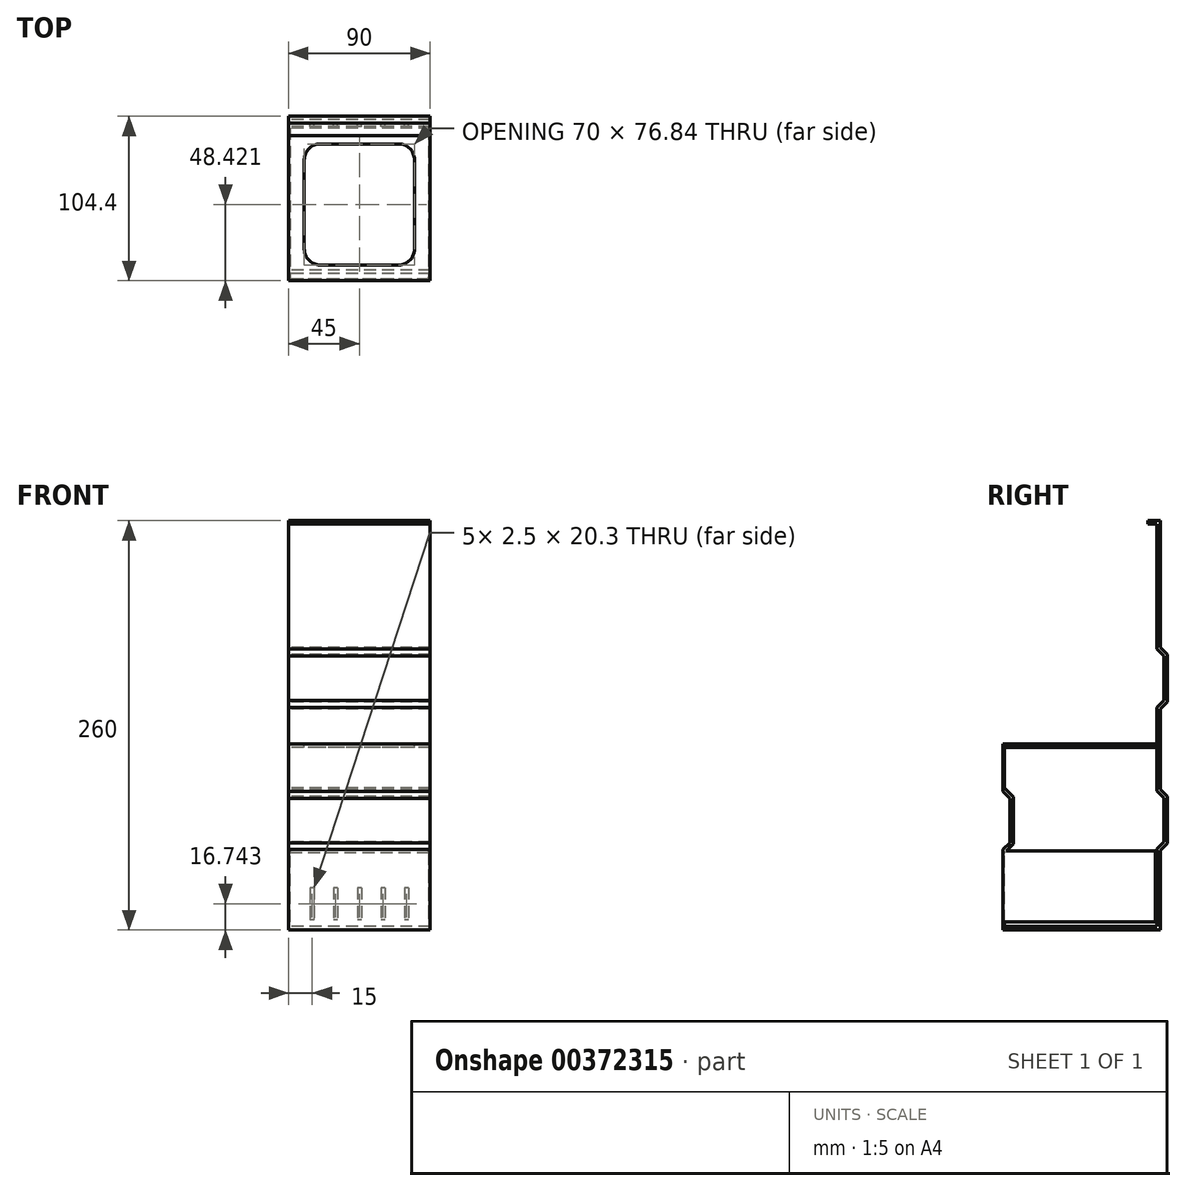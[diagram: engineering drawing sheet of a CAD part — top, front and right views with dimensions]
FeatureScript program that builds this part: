
annotation { "Feature Type Name" : "Feature", "Feature Type Description" : "" }
export const myFeature = defineFeature(function(context is Context, id is Id, definition is map)
    precondition{}
    {
        {
            var Q0;
            Q0=qCreatedBy(makeId("Right.planeOp"),FACE);
            var sketch = newSketch(context, id + "F0", { "sketchPlane" : qUnion([Q0])});
            skLineSegment(sketch, "E0.0", {"start": v(-66.12, 74.6) * mm, "end": v(-66.12, 46.42) * mm});
            skLineSegment(sketch, "E0.1", {"start": v(-63.92, 75.5) * mm, "end": v(-63.92, 45.5) * mm});
            skLineSegment(sketch, "E0.5", {"start": v(-70.52, 132.02) * mm, "end": v(-70.52, 79) * mm});
            skLineSegment(sketch, "E0.7", {"start": v(-68.32, 240.5) * mm, "end": v(-68.32, 169.9) * mm});
            skLineSegment(sketch, "E0.8", {"start": v(-66.12, 164.6) * mm, "end": v(-66.12, 136.42) * mm});
            skLineSegment(sketch, "E0.9", {"start": v(-63.92, 165.5) * mm, "end": v(-63.92, 135.5) * mm});
            skLineSegment(sketch, "E1.4", {"start": v(-68.32, 131.1) * mm, "end": v(-68.32, 79.9) * mm});
            skLineSegment(sketch, "E1.9", {"start": v(-70.52, 238.3) * mm, "end": v(-70.52, 169) * mm});
            skLineSegment(sketch, "E2.0", {"start": v(-63.92, 75.5) * mm, "end": v(-68.32, 79.9) * mm});
            skLineSegment(sketch, "E3.0", {"start": v(-66.12, 74.6) * mm, "end": v(-70.52, 79) * mm});
            skLineSegment(sketch, "E4.0", {"start": v(-68.32, 41.1) * mm, "end": v(-63.92, 45.5) * mm});
            skLineSegment(sketch, "E5.0", {"start": v(-66.12, 136.42) * mm, "end": v(-70.52, 132.02) * mm});
            skLineSegment(sketch, "E6.0", {"start": v(-63.92, 135.5) * mm, "end": v(-68.32, 131.1) * mm});
            skLineSegment(sketch, "E7.0", {"start": v(-68.32, 169.9) * mm, "end": v(-63.92, 165.5) * mm});
            skLineSegment(sketch, "E8.0", {"start": v(-70.52, 169) * mm, "end": v(-66.12, 164.6) * mm});
            skLineSegment(sketch, "E9", {"start": v(-66.12, 46.42) * mm, "end": v(-70.52, 42.02) * mm});
            skLineSegment(sketch, "E10.left", {"start": v(-168.32, -9.5) * mm, "end": v(-168.32, 41.61) * mm});
            skLineSegment(sketch, "E10.right", {"start": v(-167.32, -9.5) * mm, "end": v(-167.32, 42.61) * mm});
            skLineSegment(sketch, "E11.4", {"start": v(-161.72, 75.1) * mm, "end": v(-161.72, 45.1) * mm});
            skLineSegment(sketch, "E11.6", {"start": v(-163.92, 74.2) * mm, "end": v(-163.92, 46.01) * mm});
            skLineSegment(sketch, "E12.0", {"start": v(-166.12, 40.7) * mm, "end": v(-161.72, 45.1) * mm});
            skLineSegment(sketch, "E13.0", {"start": v(-168.32, 41.61) * mm, "end": v(-163.92, 46.01) * mm});
            skLineSegment(sketch, "E14.0", {"start": v(-163.92, 74.2) * mm, "end": v(-168.32, 78.6) * mm});
            skLineSegment(sketch, "E15.0", {"start": v(-161.72, 75.1) * mm, "end": v(-166.12, 79.5) * mm});
            skLineSegment(sketch, "E16", {"start": v(-166.12, 79.5) * mm, "end": v(-168.32, 81.7) * mm});
            skLineSegment(sketch, "E17", {"start": v(-166.12, 40.7) * mm, "end": v(-168.32, 38.48) * mm});
            skLineSegment(sketch, "E18.trimOffspring", {"start": v(-167.32, 77.6) * mm, "end": v(-167.32, 108.73) * mm});
            skLineSegment(sketch, "E19.trimOffspring", {"start": v(-168.32, 78.6) * mm, "end": v(-168.32, 108.73) * mm});
            skLineSegment(sketch, "E20", {"start": v(-68.32, 41.1) * mm, "end": v(-68.32, -9.5) * mm});
            skLineSegment(sketch, "E21.bottom", {"start": v(-68.32, -9.5) * mm, "end": v(-168.32, -9.5) * mm});
            skLineSegment(sketch, "E21.top", {"start": v(-68.32, -7.3) * mm, "end": v(-168.32, -7.3) * mm});
            skLineSegment(sketch, "E21.left", {"start": v(-68.32, -9.5) * mm, "end": v(-68.32, -7.3) * mm});
            skLineSegment(sketch, "E21.right", {"start": v(-168.32, -9.5) * mm, "end": v(-168.32, -7.3) * mm});
            skLineSegment(sketch, "E22", {"start": v(-70.52, 42.02) * mm, "end": v(-70.52, -9.5) * mm});
            skLineSegment(sketch, "E23", {"start": v(-168.32, 108.73) * mm, "end": v(-71.48, 108.73) * mm});
            skLineSegment(sketch, "E24", {"start": v(-168.32, 106.53) * mm, "end": v(-71.48, 106.53) * mm});
            skLineSegment(sketch, "E25", {"start": v(-71.48, 106.53) * mm, "end": v(-71.48, 108.73) * mm});
            skLineSegment(sketch, "E26", {"start": v(-50.44, 240.5) * mm, "end": v(-50.44, 250.5) * mm, "construction": true});
            skLineSegment(sketch, "E27", {"start": v(-50.44, 250.5) * mm, "end": v(-80.83, 250.5) * mm, "construction": true});
            skLineSegment(sketch, "E28", {"start": v(-68.32, 250.5) * mm, "end": v(-68.32, 240.5) * mm});
            skLineSegment(sketch, "E29", {"start": v(-70.52, 250.5) * mm, "end": v(-70.52, 238.3) * mm});
            skLineSegment(sketch, "E30.bottom", {"start": v(-76.32, 250.5) * mm, "end": v(-76.32, 250.5) * mm});
            skLineSegment(sketch, "E30.top", {"start": v(-76.32, 248.3) * mm, "end": v(-76.32, 248.3) * mm});
            skLineSegment(sketch, "E30.left", {"start": v(-76.32, 250.5) * mm, "end": v(-76.32, 248.3) * mm, "construction": true});
            skLineSegment(sketch, "E30.right", {"start": v(-76.32, 250.5) * mm, "end": v(-76.32, 248.3) * mm, "construction": true});
            skLineSegment(sketch, "E31.bottom", {"start": v(-76.32, 248.3) * mm, "end": v(-68.32, 248.3) * mm});
            skLineSegment(sketch, "E31.top", {"start": v(-76.32, 250.5) * mm, "end": v(-68.32, 250.5) * mm});
            skLineSegment(sketch, "E31.left", {"start": v(-76.32, 248.3) * mm, "end": v(-76.32, 250.5) * mm});
            skLineSegment(sketch, "E31.right", {"start": v(-68.32, 248.3) * mm, "end": v(-68.32, 250.5) * mm});
            skSolve(sketch);
        }
        {
            var Q0;
            Q0 = qSketchRegion(id + "F0", true);
            extrude(context, id + "F1", {"entities" : qUnion([Q0]), "depth" : 90 * mm, "offsetDistance" : 25 * mm});
        }
        {
            var Q0;
            Q0=makeQuery(id+"F1.opExtrude","SWEPT_FACE",FACE,{"disambiguationData":[OSD([sQuery(id+"F0.wireOp",EDGE,"E10.right")])]});
            var sketch = newSketch(context, id + "F2", { "sketchPlane" : qUnion([Q0])});
            skLineSegment(sketch, "E32.bottom", {"start": v(-90, 40.7) * mm, "end": v(-89, 40.7) * mm});
            skLineSegment(sketch, "E32.top", {"start": v(-90, -4.3) * mm, "end": v(-89, -4.3) * mm});
            skLineSegment(sketch, "E32.left", {"start": v(-90, 40.7) * mm, "end": v(-90, -4.3) * mm});
            skLineSegment(sketch, "E32.right", {"start": v(-89, 40.7) * mm, "end": v(-89, -4.3) * mm});
            skLineSegment(sketch, "E33.bottom", {"start": v(0, -4.3) * mm, "end": v(-1, -4.3) * mm});
            skLineSegment(sketch, "E33.top", {"start": v(0, 40.7) * mm, "end": v(-1, 40.7) * mm});
            skLineSegment(sketch, "E33.left", {"start": v(0, -4.3) * mm, "end": v(0, 40.7) * mm});
            skLineSegment(sketch, "E33.right", {"start": v(-1, -4.3) * mm, "end": v(-1, 40.7) * mm});
            skSolve(sketch);
        }
        {
            var Q0;
            Q0 = qSketchRegion(id + "F2", true);
            extrude(context, id + "F3", {"entities" : qUnion([Q0]), "operationType" : NewBodyOperationType.ADD, "depth" : 96 * mm, "offsetDistance" : 25 * mm});
        }
        {
            var Q0;
            Q0=makeQuery(id+"F1.opExtrude","SWEPT_FACE",FACE,{"disambiguationData":[OSD([sQuery(id+"F0.wireOp",EDGE,"E23")])]});
            var sketch = newSketch(context, id + "F4", { "sketchPlane" : qUnion([Q0])});
            skLineSegment(sketch, "E34.bottom", {"start": v(80, -81.48) * mm, "end": v(10, -81.48) * mm});
            skLineSegment(sketch, "E34.top", {"start": v(80, -158.32) * mm, "end": v(10, -158.32) * mm});
            skLineSegment(sketch, "E34.left", {"start": v(80, -81.48) * mm, "end": v(80, -158.32) * mm});
            skLineSegment(sketch, "E34.right", {"start": v(10, -81.48) * mm, "end": v(10, -158.32) * mm});
            skPoint(sketch, "E34.middle", {"position": v(45, -119.9) * mm});
            skPoint(sketch, "E34.middle.positionSnap0", {"position": v(0, -119.9) * mm});
            skPoint(sketch, "E34.centerSnap0", {"position": v(0, -119.9) * mm});
            skSolve(sketch);
        }
        {
            var Q0;
            Q0 = qSketchRegion(id + "F4", true);
            extrude(context, id + "F5", {"entities" : qUnion([Q0]), "operationType" : NewBodyOperationType.REMOVE, "oppositeDirection" : true, "depth" : 25 * mm, "offsetDistance" : 25 * mm});
        }
        {
            var Q0;
            Q0=makeQuery(id+"F5.boolean.opBoolean","COPY",EDGE,{"derivedFrom":makeQuery(id+"F5.opExtrude","SWEPT_EDGE",EDGE,{"disambiguationData":[OSD([sQuery(id+"F4.wireOp",EDGE,"E34.bottom"),sQuery(id+"F4.wireOp",EDGE,"E34.right")])]})});
            var Q1;
            Q1=makeQuery(id+"F5.boolean.opBoolean","COPY",EDGE,{"derivedFrom":makeQuery(id+"F5.opExtrude","SWEPT_EDGE",EDGE,{"disambiguationData":[OSD([sQuery(id+"F4.wireOp",EDGE,"E34.top"),sQuery(id+"F4.wireOp",EDGE,"E34.right")])]})});
            var Q2;
            Q2=makeQuery(id+"F5.boolean.opBoolean","COPY",EDGE,{"derivedFrom":makeQuery(id+"F5.opExtrude","SWEPT_EDGE",EDGE,{"disambiguationData":[OSD([sQuery(id+"F4.wireOp",EDGE,"E34.bottom"),sQuery(id+"F4.wireOp",EDGE,"E34.left")])]})});
            var Q3;
            Q3=makeQuery(id+"F5.boolean.opBoolean","COPY",EDGE,{"derivedFrom":makeQuery(id+"F5.opExtrude","SWEPT_EDGE",EDGE,{"disambiguationData":[OSD([sQuery(id+"F4.wireOp",EDGE,"E34.top"),sQuery(id+"F4.wireOp",EDGE,"E34.left")])]})});
            fillet(context, id + "F6", {"entities" : qUnion([Q0, Q1, Q2, Q3]), "radius" : 10 * mm, "tangentPropagation" : true, "allowEdgeOverflow" : false});
        }
        {
            var Q0;
            Q0=makeQuery(id+"F1.opExtrude","SWEPT_FACE",FACE,{"disambiguationData":[OSD([sQuery(id+"F0.wireOp",EDGE,"E20"),sQuery(id+"F0.wireOp",EDGE,"E21.left")])]});
            var sketch = newSketch(context, id + "F7", { "sketchPlane" : qUnion([Q0])});
            skLineSegment(sketch, "E35.bottom", {"start": v(-76.25, 17.4) * mm, "end": v(-73.75, 17.4) * mm});
            skLineSegment(sketch, "E35.top", {"start": v(-76.25, -2.9) * mm, "end": v(-73.75, -2.9) * mm});
            skLineSegment(sketch, "E35.left", {"start": v(-76.25, 17.4) * mm, "end": v(-76.25, -2.9) * mm});
            skLineSegment(sketch, "E35.right", {"start": v(-73.75, 17.4) * mm, "end": v(-73.75, -2.9) * mm});
            skLineSegment(sketch, "E36.1.0.0", {"start": v(-58.75, 17.4) * mm, "end": v(-58.75, -2.9) * mm});
            skLineSegment(sketch, "E36.1.0.1", {"start": v(-61.25, 17.4) * mm, "end": v(-61.25, -2.9) * mm});
            skLineSegment(sketch, "E36.1.0.2", {"start": v(-61.25, -2.9) * mm, "end": v(-58.75, -2.9) * mm});
            skLineSegment(sketch, "E36.1.0.3", {"start": v(-61.25, 17.4) * mm, "end": v(-58.75, 17.4) * mm});
            skLineSegment(sketch, "E36.2.0.0", {"start": v(-43.75, 17.4) * mm, "end": v(-43.75, -2.9) * mm});
            skLineSegment(sketch, "E36.2.0.1", {"start": v(-46.25, 17.4) * mm, "end": v(-46.25, -2.9) * mm});
            skLineSegment(sketch, "E36.2.0.2", {"start": v(-46.25, -2.9) * mm, "end": v(-43.75, -2.9) * mm});
            skLineSegment(sketch, "E36.2.0.3", {"start": v(-46.25, 17.4) * mm, "end": v(-43.75, 17.4) * mm});
            skLineSegment(sketch, "E36.3.0.0", {"start": v(-28.75, 17.4) * mm, "end": v(-28.75, -2.9) * mm});
            skLineSegment(sketch, "E36.3.0.1", {"start": v(-31.25, 17.4) * mm, "end": v(-31.25, -2.9) * mm});
            skLineSegment(sketch, "E36.3.0.2", {"start": v(-31.25, -2.9) * mm, "end": v(-28.75, -2.9) * mm});
            skLineSegment(sketch, "E36.3.0.3", {"start": v(-31.25, 17.4) * mm, "end": v(-28.75, 17.4) * mm});
            skLineSegment(sketch, "E36.4.0.0", {"start": v(-13.75, 17.4) * mm, "end": v(-13.75, -2.9) * mm});
            skLineSegment(sketch, "E36.4.0.1", {"start": v(-16.25, 17.4) * mm, "end": v(-16.25, -2.9) * mm});
            skLineSegment(sketch, "E36.4.0.2", {"start": v(-16.25, -2.9) * mm, "end": v(-13.75, -2.9) * mm});
            skLineSegment(sketch, "E36.4.0.3", {"start": v(-16.25, 17.4) * mm, "end": v(-13.75, 17.4) * mm});
            skLineSegment(sketch, "E36.direction1", {"start": v(-76.25, -2.9) * mm, "end": v(-61.25, -2.9) * mm, "construction": true});
            skSolve(sketch);
        }
        {
            var Q0;
            Q0 = qSketchRegion(id + "F7", true);
            extrude(context, id + "F8", {"entities" : qUnion([Q0]), "operationType" : NewBodyOperationType.REMOVE, "oppositeDirection" : true, "depth" : 25 * mm, "offsetDistance" : 25 * mm});
        }
    });
